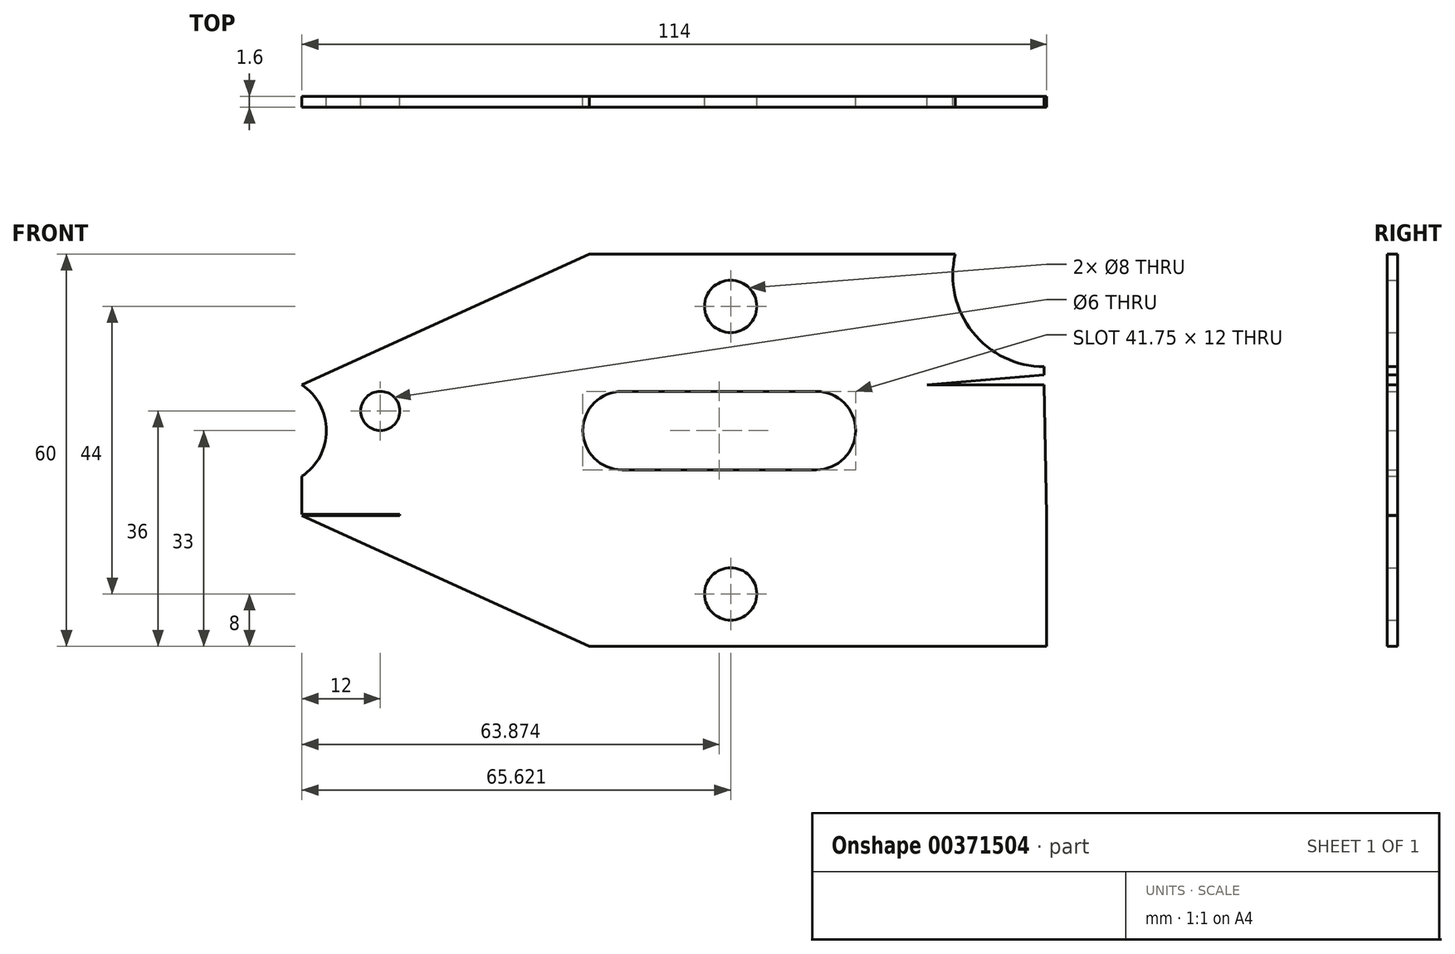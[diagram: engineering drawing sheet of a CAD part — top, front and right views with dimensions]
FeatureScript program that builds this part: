
annotation { "Feature Type Name" : "Feature", "Feature Type Description" : "" }
export const myFeature = defineFeature(function(context is Context, id is Id, definition is map)
    precondition{}
    {
        {
            var Q0;
            Q0=qCreatedBy(makeId("Front.planeOp"),FACE);
            var sketch = newSketch(context, id + "F0", { "sketchPlane" : qUnion([Q0])});
            skLineSegment(sketch, "E0.left", {"start": v(0, 0) * mm, "end": v(-0.38, 20) * mm});
            skLineSegment(sketch, "E1", {"start": v(-0.38, 21.5) * mm, "end": v(-0.38, 22.76) * mm});
            skLineSegment(sketch, "E2", {"start": v(-14, 40) * mm, "end": v(-70, 40) * mm});
            skLineSegment(sketch, "E3", {"start": v(-70, 40) * mm, "end": v(-114, 20) * mm});
            skLineSegment(sketch, "E4", {"start": v(0, 0) * mm, "end": v(0, -20) * mm});
            skLineSegment(sketch, "E5", {"start": v(0, -20) * mm, "end": v(-70, -20) * mm});
            skLineSegment(sketch, "E6", {"start": v(-70, -20) * mm, "end": v(-114, 0) * mm});
            skLineSegment(sketch, "E7.bottom", {"start": v(-35.25, 19) * mm, "end": v(-65, 19) * mm});
            skLineSegment(sketch, "E7.top", {"start": v(-35.25, 7) * mm, "end": v(-65, 7) * mm});
            skLineSegment(sketch, "E7.left", {"start": v(-29.25, 13) * mm, "end": v(-29.25, 13) * mm});
            skLineSegment(sketch, "E7.right", {"start": v(-71, 13) * mm, "end": v(-71, 13) * mm});
            skArc(sketch, "E8.filletArc", {"start": v(-65, 19) * mm, "mid": v(-69.24, 17.24) * mm, "end": v(-71, 13) * mm});
            skArc(sketch, "E9.filletArc", {"start": v(-71, 13) * mm, "mid": v(-69.24, 8.76) * mm, "end": v(-65, 7) * mm});
            skArc(sketch, "E10.filletArc", {"start": v(-35.25, 7) * mm, "mid": v(-31.01, 8.76) * mm, "end": v(-29.25, 13) * mm});
            skArc(sketch, "E11.filletArc", {"start": v(-29.25, 13) * mm, "mid": v(-31.01, 17.24) * mm, "end": v(-35.25, 19) * mm});
            skLineSegment(sketch, "E12", {"start": v(-71, 13) * mm, "end": v(-29.25, 13) * mm, "construction": true});
            skLineSegment(sketch, "E13", {"start": v(-35.25, 19) * mm, "end": v(-35.25, 7) * mm, "construction": true});
            skLineSegment(sketch, "E14", {"start": v(-65, 7) * mm, "end": v(-65, 19) * mm, "construction": true});
            skArc(sketch, "E15", {"start": v(-14, 40) * mm, "mid": v(-11.36, 28.08) * mm, "end": v(-0.38, 22.76) * mm});
            skLineSegment(sketch, "E16", {"start": v(-48.38, 36.21) * mm, "end": v(-48.38, -21.7) * mm, "construction": true});
            skCircle(sketch, "E17", {"center": v(-48.38, 32) * mm, "radius": 4 * mm});
            skCircle(sketch, "E18", {"center": v(-48.38, -12) * mm, "radius": 4 * mm});
            skLineSegment(sketch, "E19", {"start": v(-0.38, 21.5) * mm, "end": v(-18.32, 20) * mm});
            skLineSegment(sketch, "E20", {"start": v(-18.32, 20) * mm, "end": v(-0.38, 20) * mm});
            skCircle(sketch, "E21", {"center": v(-102, 16) * mm, "radius": 3 * mm});
            skLineSegment(sketch, "E22", {"start": v(0, 0) * mm, "end": v(-135.35, 0) * mm, "construction": true});
            skLineSegment(sketch, "E23", {"start": v(-114, 6) * mm, "end": v(-114, 0.2) * mm});
            skArc(sketch, "E24", {"start": v(-114, 6) * mm, "mid": v(-110.23, 13) * mm, "end": v(-114, 20) * mm});
            skLineSegment(sketch, "E25", {"start": v(-114, 0) * mm, "end": v(-99, 0) * mm});
            skLineSegment(sketch, "E26", {"start": v(-99, 0) * mm, "end": v(-99, 0.2) * mm});
            skLineSegment(sketch, "E27", {"start": v(-99, 0.2) * mm, "end": v(-114, 0.2) * mm});
            skSolve(sketch);
        }
        {
            var Q0;
            Q0=makeQuery(id+"F0.imprint","IMPRINT",FACE,{"disambiguationData":[TD([[makeQuery(id+"F0.imprint","IMPRINT",EDGE,{"derivedFrom":sQuery(id+"F0.wireOp",EDGE,"E0.left")}),1.0]])]});
            extrude(context, id + "F1", {"entities" : qUnion([Q0]), "depth" : 1.6 * mm});
        }
    });
